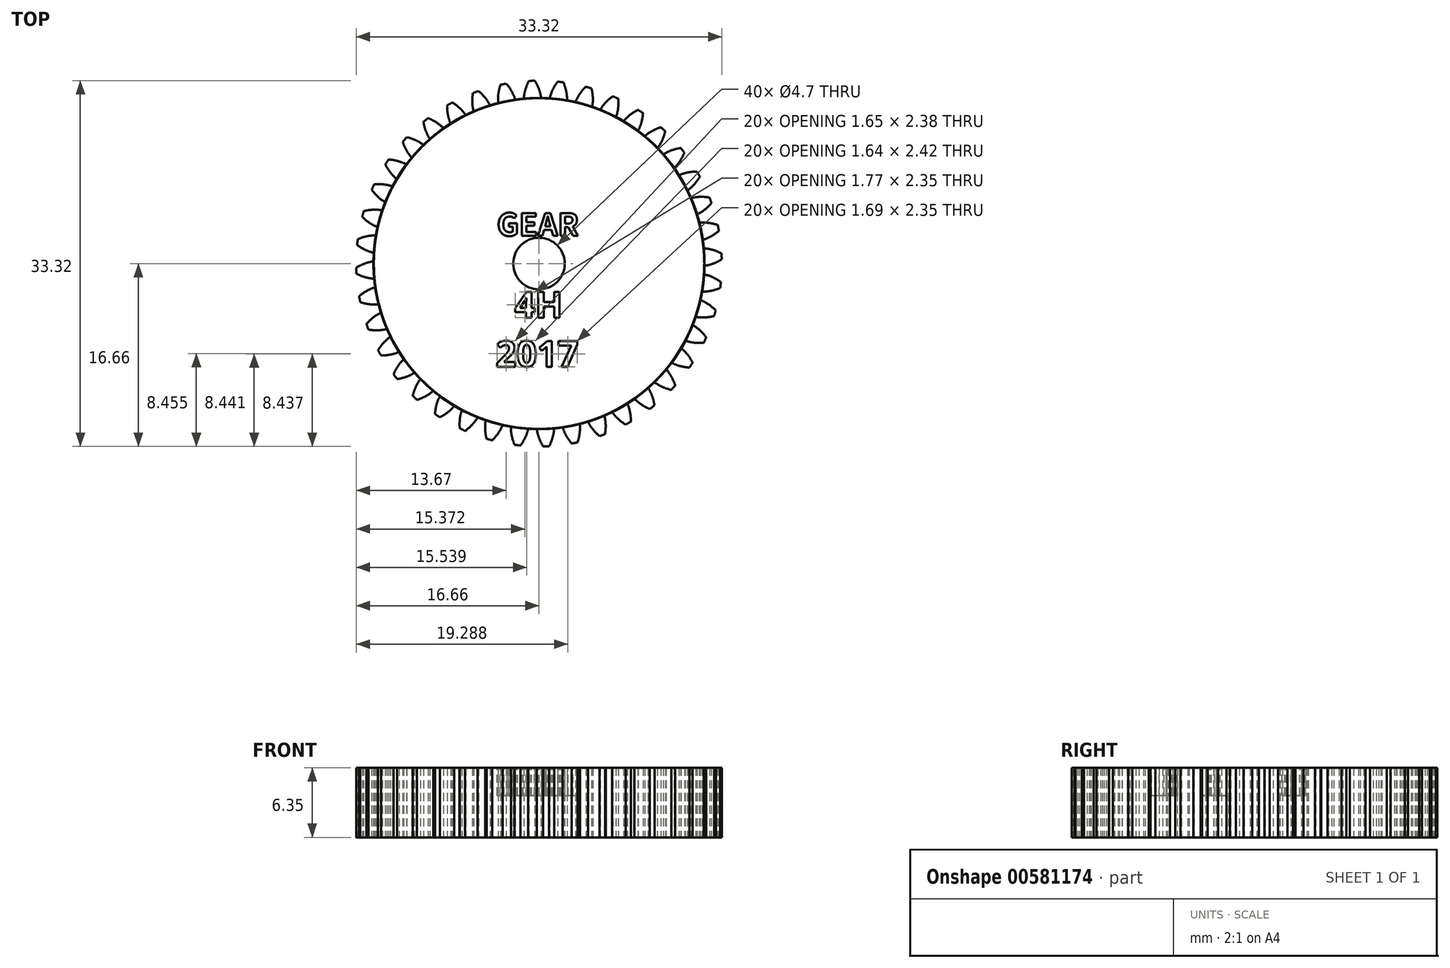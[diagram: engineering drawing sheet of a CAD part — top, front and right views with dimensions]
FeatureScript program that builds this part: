
annotation { "Feature Type Name" : "Feature", "Feature Type Description" : "" }
export const myFeature = defineFeature(function(context is Context, id is Id, definition is map)
    precondition{}
    {
        {
            var Q0;
            Q0=qCreatedBy(makeId("Top.planeOp"),FACE);
            var sketch = newSketch(context, id + "F0", { "sketchPlane" : qUnion([Q0])});
            skCircle(sketch, "E0", {"center": v(0, 0) * mm, "radius": 15.88 * mm, "construction": true});
            skCircle(sketch, "E1", {"center": v(0, 0) * mm, "radius": 15.07 * mm});
            skCircle(sketch, "E2", {"center": v(0, 0) * mm, "radius": 16.66 * mm, "construction": true});
            skLineSegment(sketch, "E3", {"start": v(0, 0) * mm, "end": v(0, 22.62) * mm, "construction": true});
            skLineSegment(sketch, "E4", {"start": v(0, 0) * mm, "end": v(-1.16, 29.54) * mm, "construction": true});
            skCircle(sketch, "E5", {"center": v(0, 15.88) * mm, "radius": 3.96 * mm, "construction": true});
            skLineSegment(sketch, "E6", {"start": v(0, 15.88) * mm, "end": v(-14.9, 15.88) * mm, "construction": true});
            skLineSegment(sketch, "E7", {"start": v(0, 15.88) * mm, "end": v(-16.96, 9.7) * mm, "construction": true});
            skCircle(sketch, "E8", {"center": v(-3.72, 14.52) * mm, "radius": 3.96 * mm, "construction": true});
            skArc(sketch, "E9", {"start": v(0, 15.88) * mm, "mid": v(-0.17, 16.28) * mm, "end": v(-0.39, 16.66) * mm});
            skArc(sketch, "E10", {"start": v(0.2, 15.07) * mm, "mid": v(0.12, 15.48) * mm, "end": v(0, 15.87) * mm});
            skArc(sketch, "E11.MirrorCS", {"start": v(-1.25, 15.83) * mm, "mid": v(-1.1, 16.24) * mm, "end": v(-0.92, 16.64) * mm});
            skArc(sketch, "E12.MirrorCS", {"start": v(-1.38, 15.01) * mm, "mid": v(-1.34, 15.42) * mm, "end": v(-1.25, 15.83) * mm});
            skArc(sketch, "E13", {"start": v(-0.92, 16.64) * mm, "mid": v(-0.65, 16.64) * mm, "end": v(-0.39, 16.66) * mm});
            skCircle(sketch, "E14", {"center": v(0, 0) * mm, "radius": 2.35 * mm});
            skSolve(sketch);
        }
        {
            var Q0;
            {var subQ0=sQuery(id+"F0.wireOp",EDGE,"E1");var subQ1=makeQuery(id+"F0.imprint","INTERSECT",VERTEX,{"derivedFrom":[subQ0,sQuery(id+"F0.wireOp",EDGE,"E10")]});Q0=makeQuery(id+"F0.imprint","IMPRINT",FACE,{"disambiguationData":[TD([[makeQuery(id+"F0.imprint","IMPRINT",EDGE,{"disambiguationData":[TD([[subQ1,-1.0]])],"derivedFrom":subQ0}),1.0]])]});}
            var Q1;
            Q1=makeQuery(id+"F0.imprint","IMPRINT",FACE,{"disambiguationData":[TD([[makeQuery(id+"F0.imprint","IMPRINT",EDGE,{"derivedFrom":sQuery(id+"F0.wireOp",EDGE,"E9")}),1.0]])]});
            extrude(context, id + "F1", {"entities" : qUnion([Q0, Q1]), "depth" : 6.35 * mm, "offsetDistance" : 25.4 * mm});
        }
        {
            var Q0;
            Q0=makeQuery(id+"F1.opExtrude","SWEPT_BODY",BODY,{"disambiguationData":[OSD([sQuery(id+"F0.wireOp",EDGE,"E1"),sQuery(id+"F0.wireOp",EDGE,"E9"),sQuery(id+"F0.wireOp",EDGE,"E10"),sQuery(id+"F0.wireOp",EDGE,"E11.MirrorCS"),sQuery(id+"F0.wireOp",EDGE,"E12.MirrorCS"),sQuery(id+"F0.wireOp",EDGE,"E13")])]});
            var Q1;
            Q1=makeQuery(id+"F1.opExtrude","SWEPT_FACE",FACE,{"disambiguationData":[OSD([sQuery(id+"F0.wireOp",EDGE,"E1")])]});
            circularPattern(context, id + "F2", {"entities" : qUnion([Q0]), "axis" : qUnion([Q1]), "angle" : 360 * degree, "instanceCount" : 40, "equalSpace" : true});
        }
        {
            var Q0;
            Q0=makeQuery(id+"F2.opPattern","COPY",FACE,{"derivedFrom":makeQuery(id+"F1.opExtrude","CAP_FACE",FACE,{"disambiguationData":[OSD([sQuery(id+"F0.wireOp",EDGE,"E1"),sQuery(id+"F0.wireOp",EDGE,"E9"),sQuery(id+"F0.wireOp",EDGE,"E10"),sQuery(id+"F0.wireOp",EDGE,"E11.MirrorCS"),sQuery(id+"F0.wireOp",EDGE,"E12.MirrorCS"),sQuery(id+"F0.wireOp",EDGE,"E13"),sQuery(id+"F0.wireOp",EDGE,"E14")])],"isStart":false}),"instanceName":"20"});
            var sketch = newSketch(context, id + "F3", { "sketchPlane" : qUnion([Q0])});
            skText(sketch, "E15", { "text": "GEAR", "fontName": "NotoSansCJKtc-Bold.otf"});
            skText(sketch, "E16", { "text": "  4H\n2017", "fontName": "OpenSans-Bold.ttf"});
            const initialGuessF3  = {"E15": [-0.00383, 0.00253, 1, 0, 0.00202], "E16": [-0.00394, -0.00492, 1, 0, 0.00237]};
            skSetInitialGuess(sketch, initialGuessF3);
            skSolve(sketch);
        }
        {
            var Q0;
            Q0 = qSketchRegion(id + "F3", true);
            extrude(context, id + "F4", {"entities" : qUnion([Q0]), "operationType" : NewBodyOperationType.REMOVE, "oppositeDirection" : true, "depth" : 2.54 * mm, "offsetDistance" : 25.4 * mm});
        }
    });
